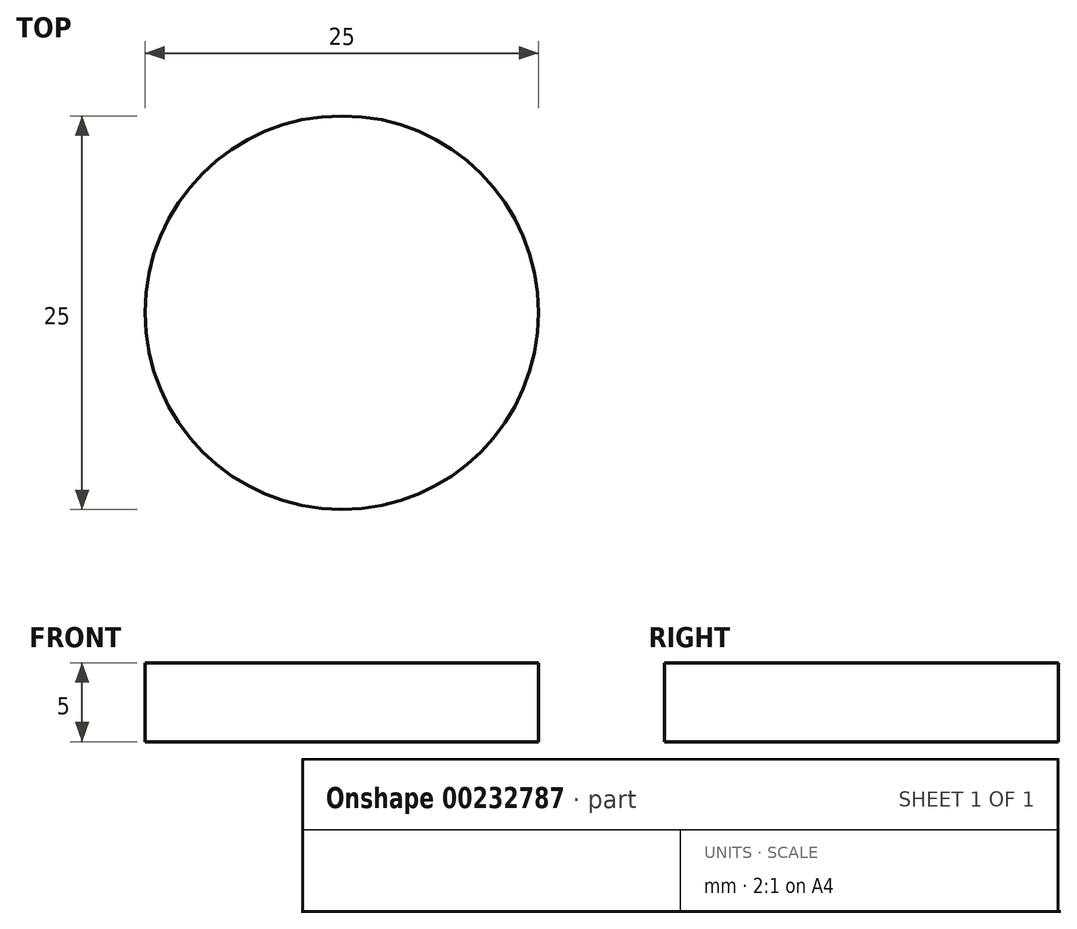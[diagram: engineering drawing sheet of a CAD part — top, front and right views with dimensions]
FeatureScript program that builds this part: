
annotation { "Feature Type Name" : "Feature", "Feature Type Description" : "" }
export const myFeature = defineFeature(function(context is Context, id is Id, definition is map)
    precondition{}
    {
        {
            var Q0;
            Q0=qCreatedBy(makeId("Top.planeOp"),FACE);
            var sketch = newSketch(context, id + "F0", { "sketchPlane" : qUnion([Q0])});
            skCircle(sketch, "E0", {"center": v(0, 0) * mm, "radius": 12.5 * mm});
            skSolve(sketch);
        }
        {
            var Q0;
            Q0=makeQuery(id+"F0.imprint","IMPRINT",FACE,{"disambiguationData":[TD([[makeQuery(id+"F0.imprint","IMPRINT",EDGE,{"derivedFrom":sQuery(id+"F0.wireOp",EDGE,"E0")}),1.0]])]});
            extrude(context, id + "F1", {"entities" : qUnion([Q0]), "depth" : 5 * mm});
        }
    });
